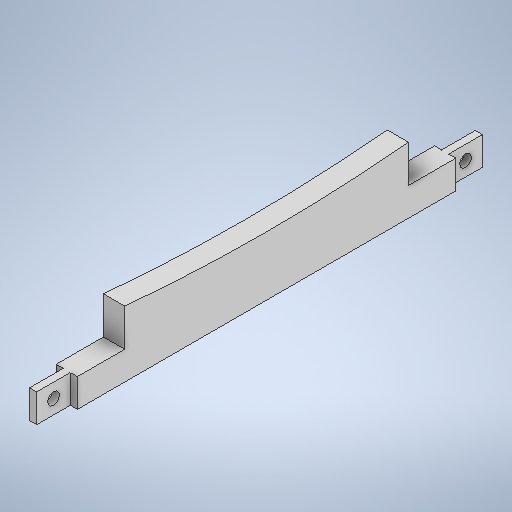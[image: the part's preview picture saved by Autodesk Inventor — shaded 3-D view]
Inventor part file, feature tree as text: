
AUTODESK INVENTOR PART (.ipt)
format: ipt  version: 2025.1 (Build 291241000, 241)  size: 281,600 bytes
history: native  units: in
note: dims shown in document units (in); Inventor stores cm internally (conversion verified against a paired STEP export)
features: extrude x5, sketch x4, fillet x1
ambient origin geometry x8: Origin, YZ Plane, XZ Plane, XY Plane, X Axis, Y Axis, Z Axis, Center Point
bodies: Solid1 (feature_tree)
feature tree (10):
  sketch  "Sketch1"  dims[d6=0.3in d7=0.0in d8=0.75in d9=0.0in]
  extrude  "Extrusion1"  Depth=0.3in TaperAngle=0.0deg
  extrude  "Extrusion2"  Depth=0.5in TaperAngle=0.0deg
  extrude  "Extrusion3"  Depth=0.5in TaperAngle=0.0deg
  extrude  "Extrusion4"  Depth=4.0in
  fillet  "Fillet1"  Radius=0.075in
  extrude  "Extrusion5"  Depth=0.075in
  sketch  "Sketch2"  dims[d12=0.125in d13=0.5in d14=0.0in]
  sketch  "Sketch3"  dims[d15=0.125in d16=0.5in d17=0.0in]
  sketch  "Sketch4"  dims[d18=0.175in d19=4.0in d20=0.075in d21=0.075in d22=0.075in d23=0.075in d24=0.075in d25=0.075in d26=0.5in d27=0.5in d28=0.5in d29=0.5in d30=1.0in d31=0.0in d32=0.5in d33=0.0344in]
